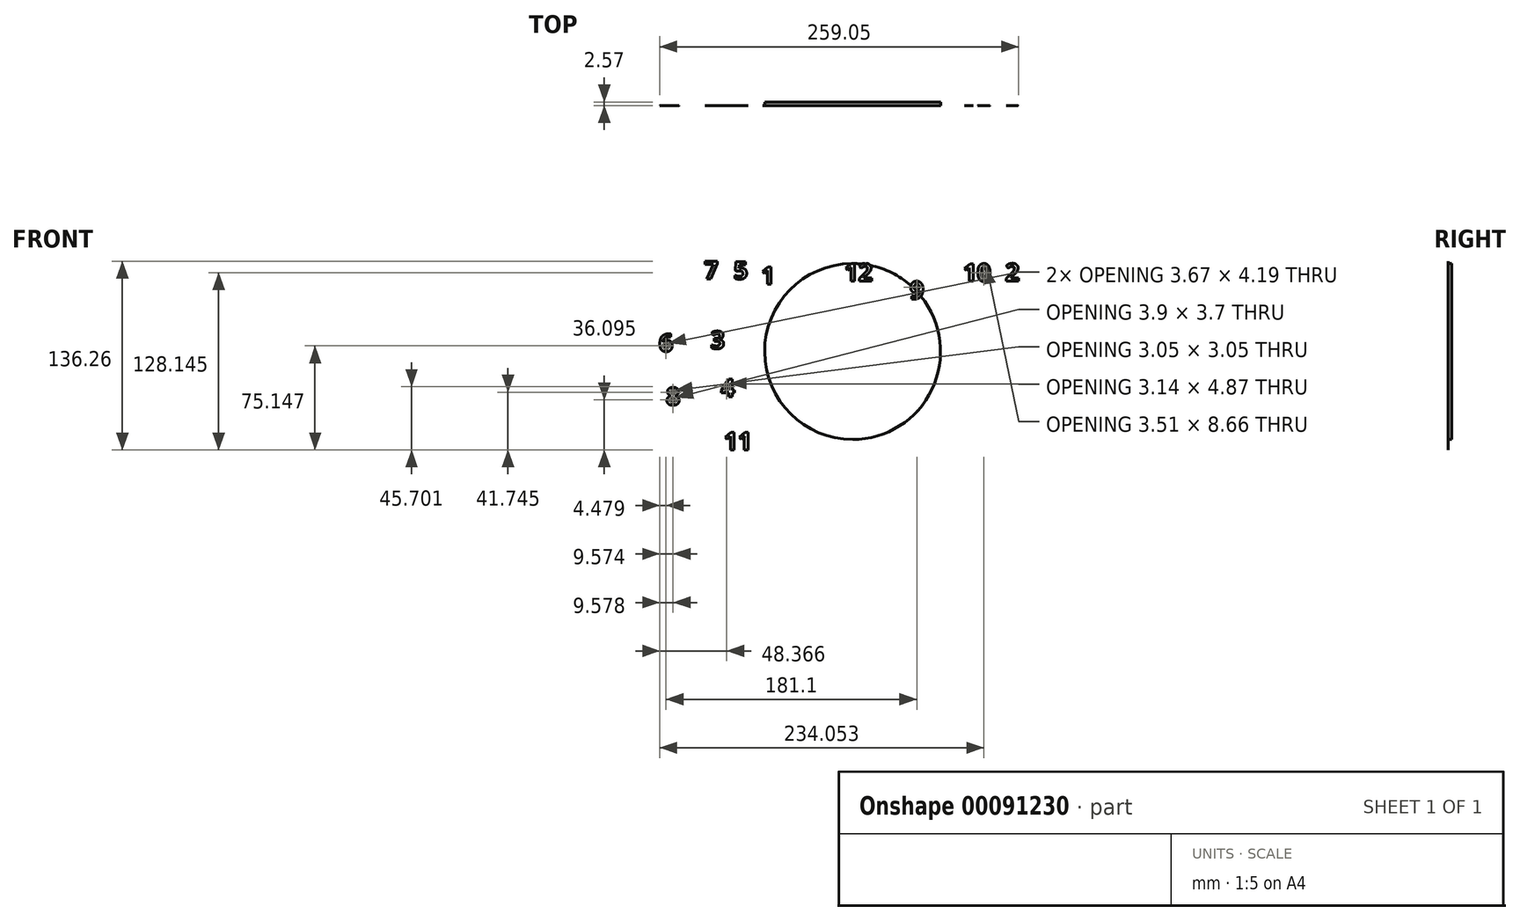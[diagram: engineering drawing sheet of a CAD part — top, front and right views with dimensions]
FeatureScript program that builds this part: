
annotation { "Feature Type Name" : "Feature", "Feature Type Description" : "" }
export const myFeature = defineFeature(function(context is Context, id is Id, definition is map)
    precondition{}
    {
        {
            var Q0;
            Q0=qCreatedBy(makeId("Front.planeOp"),FACE);
            var sketch = newSketch(context, id + "F0", { "sketchPlane" : qUnion([Q0])});
            skCircle(sketch, "E0", {"center": v(0, 0) * mm, "radius": 63.5 * mm});
            skSolve(sketch);
        }
        {
            var Q0;
            Q0 = qSketchRegion(id + "F0", true);
            extrude(context, id + "F1", {"entities" : qUnion([Q0]), "depth" : 2.54 * mm});
        }
        {
            var Q0;
            Q0=makeQuery(id+"F1.opExtrude","CAP_FACE",FACE,{"disambiguationData":[OSD([sQuery(id+"F0.wireOp",EDGE,"E0")])],"isStart":false});
            var sketch = newSketch(context, id + "F2", { "sketchPlane" : qUnion([Q0])});
            skCircle(sketch, "E1", {"center": v(0, 0) * mm, "radius": 50.8 * mm, "construction": true});
            skLineSegment(sketch, "E2", {"start": v(0, 0) * mm, "end": v(0, 50.8) * mm, "construction": true});
            skLineSegment(sketch, "E3.1.0", {"start": v(0, 0) * mm, "end": v(-25.4, 44) * mm, "construction": true});
            skLineSegment(sketch, "E3.2.0", {"start": v(0, 0) * mm, "end": v(-44, 25.4) * mm, "construction": true});
            skLineSegment(sketch, "E3.3.0", {"start": v(0, 0) * mm, "end": v(-50.8, 0) * mm, "construction": true});
            skLineSegment(sketch, "E3.4.0", {"start": v(0, 0) * mm, "end": v(-44, -25.4) * mm, "construction": true});
            skLineSegment(sketch, "E3.5.0", {"start": v(0, 0) * mm, "end": v(-25.4, -44) * mm, "construction": true});
            skLineSegment(sketch, "E3.6.0", {"start": v(0, 0) * mm, "end": v(0, -50.8) * mm, "construction": true});
            skLineSegment(sketch, "E3.7.0", {"start": v(0, 0) * mm, "end": v(25.4, -44) * mm, "construction": true});
            skLineSegment(sketch, "E3.8.0", {"start": v(0, 0) * mm, "end": v(44, -25.4) * mm, "construction": true});
            skLineSegment(sketch, "E3.9.0", {"start": v(0, 0) * mm, "end": v(50.8, 0) * mm, "construction": true});
            skLineSegment(sketch, "E3.10.0", {"start": v(0, 0) * mm, "end": v(44, 25.4) * mm, "construction": true});
            skLineSegment(sketch, "E3.11.0", {"start": v(0, 0) * mm, "end": v(25.4, 44) * mm, "construction": true});
            skText(sketch, "E4", { "text": "12", "fontName": "OpenSans-Bold.ttf"});
            skText(sketch, "E5", { "text": "1", "fontName": "OpenSans-Bold.ttf"});
            skText(sketch, "E6", { "text": "2", "fontName": "OpenSans-Bold.ttf"});
            skText(sketch, "E7", { "text": "3", "fontName": "OpenSans-Bold.ttf"});
            skText(sketch, "E8", { "text": "4", "fontName": "OpenSans-Bold.ttf"});
            skText(sketch, "E9", { "text": "5", "fontName": "OpenSans-Bold.ttf"});
            skText(sketch, "E10", { "text": "6", "fontName": "OpenSans-Bold.ttf"});
            skText(sketch, "E11", { "text": "7", "fontName": "OpenSans-Bold.ttf"});
            skText(sketch, "E12", { "text": "8", "fontName": "OpenSans-Bold.ttf"});
            skText(sketch, "E13", { "text": "9", "fontName": "OpenSans-Bold.ttf"});
            skText(sketch, "E14", { "text": "10", "fontName": "OpenSans-Bold.ttf"});
            skText(sketch, "E15", { "text": "11", "fontName": "OpenSans-Bold.ttf"});
            skLineSegment(sketch, "E16", {"start": v(79.74, 57.1) * mm, "end": v(99.25, 57.1) * mm, "construction": true});
            skLineSegment(sketch, "E17", {"start": v(99.25, 57.1) * mm, "end": v(79.74, 57.1) * mm, "construction": true});
            skLineSegment(sketch, "E18", {"start": v(110.33, 57.3) * mm, "end": v(119.84, 57.3) * mm, "construction": true});
            skLineSegment(sketch, "E19", {"start": v(119.84, 57.3) * mm, "end": v(110.33, 57.3) * mm, "construction": true});
            skLineSegment(sketch, "E20", {"start": v(41.39, 44.4) * mm, "end": v(50.84, 44.4) * mm, "construction": true});
            skLineSegment(sketch, "E21", {"start": v(-5.86, 57.3) * mm, "end": v(13.72, 57.3) * mm, "construction": true});
            skLineSegment(sketch, "E22", {"start": v(13.72, 57.3) * mm, "end": v(-5.86, 57.3) * mm, "construction": true});
            skLineSegment(sketch, "E23", {"start": v(-66.1, 54.89) * mm, "end": v(-58.81, 54.89) * mm, "construction": true});
            skLineSegment(sketch, "E24", {"start": v(-85.74, 58.68) * mm, "end": v(-76.46, 58.68) * mm, "construction": true});
            skLineSegment(sketch, "E25", {"start": v(-107.13, 58.93) * mm, "end": v(-97.62, 58.93) * mm, "construction": true});
            skLineSegment(sketch, "E26", {"start": v(-134.67, -32.29) * mm, "end": v(-125.2, -32.29) * mm, "construction": true});
            skLineSegment(sketch, "E27", {"start": v(-125.2, -32.29) * mm, "end": v(-134.67, -32.29) * mm, "construction": true});
            const initialGuessF2  = {"E4": [-0.00586, 0.05095, 1, 0, 0.0127], "E5": [-0.0661, 0.04854, 1, 0, 0.0127], "E6": [0.11033, 0.05095, 1, 0, 0.0127], "E7": [-0.10247, 0.00206, 1, 0, 0.0127], "E8": [-0.09506, -0.03251, 1, 0, 0.0127], "E9": [-0.08574, 0.05233, 1, 0, 0.0127], "E10": [-0.13983, 0, 1, 0, 0.0127], "E11": [-0.10713, 0.05258, 1, 0, 0.0127], "E12": [-0.13467, -0.03864, 1, 0, 0.0127], "E13": [0.04139, 0.03804, 1, 0, 0.0127], "E14": [0.07974, 0.05074, 1, 0, 0.0127], "E15": [-0.09287, -0.0711, 1, 0, 0.0127]};
            skSetInitialGuess(sketch, initialGuessF2);
            skSolve(sketch);
        }
        {
            var Q0;
            Q0 = qSketchRegion(id + "F2", true);
            extrude(context, id + "F3", {"entities" : qUnion([Q0]), "depth" : 0.03 * mm});
        }
    });
